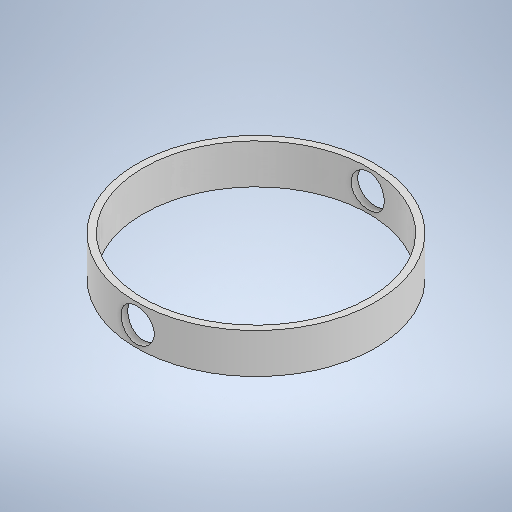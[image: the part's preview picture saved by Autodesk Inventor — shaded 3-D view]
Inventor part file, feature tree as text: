
AUTODESK INVENTOR PART (.ipt)
format: ipt  version: 2025.1 (Build 291241000, 241)  size: 265,728 bytes
history: native  units: mm
features: extrude x2, sketch x2, plane x1, mirror x1
ambient origin geometry x8: Origin, YZ Plane, XZ Plane, XY Plane, X Axis, Y Axis, Z Axis, Center Point
bodies: Solid1 (feature_tree)
feature tree (6):
  extrude  "Extrusion1"  Depth=17.0mm
  plane  "Work Plane1"
  extrude  "Extrusion2"  Depth=9.0mm
  mirror  "Mirror1"
  sketch  "Sketch1"  dims[d0=18.0mm d1=17.0mm]
  sketch  "Sketch2"  dims[d2=3.0mm d3=0.0mm d4=9.0mm d5=2.5mm d6=3.0mm d7=0.0mm]
